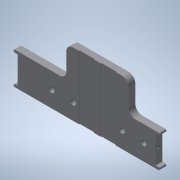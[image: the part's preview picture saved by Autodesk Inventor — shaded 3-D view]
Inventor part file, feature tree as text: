
AUTODESK INVENTOR PART (.ipt)
format: ipt  version: 2022 (Build 260153000, 153)  size: 202,752 bytes
history: native  units: mm
features: sketch x7, extrude x4, fillet x3, hole x3, plane x1, pattern_linear x1
ambient origin geometry x8: Origin, YZ Plane, XZ Plane, XY Plane, X Axis, Y Axis, Z Axis, Center Point
bodies: Volumenkörper1 (feature_tree)
feature tree (19):
  extrude  "Extrusion1"  Depth=24.0mm
  extrude  "Extrusion2"  Depth=23.0mm
  extrude  "Extrusion3"  Depth=2.0mm
  fillet  "Rundung1"  Radius=2.0mm
  fillet  "Rundung2"  Radius=3.0mm
  extrude  "Extrusion4"  Depth=2.0mm
  hole  "Bohrung2"  [1 undecoded]
  hole  "Bohrung3"  [1 undecoded]
  hole  "Bohrung4"  [1 undecoded]
  plane  "Arbeitsebene1"
  pattern_linear  "Rechteckige Anordnung1"  Spacing1=12.0mm  [1 undecoded]
  fillet  "Rundung3"  Radius=26.0mm
  sketch  "Skizze1"  dims[d0=108.0mm d1=24.0mm]
  sketch  "Skizze2"  dims[d2=39.0mm d3=23.0mm]
  sketch  "Skizze3"  dims[d5=5.0mm d6=0.0mm d7=2.0mm d8=2.0mm d9=3.0mm d10=0.0mm]
  sketch  "Skizze4"  dims[d11=2.0mm d12=2.0mm]
  sketch  "Skizze6"  dims[d13=3.0mm d14=0.0mm d15=1.0mm]
  sketch  "Skizze7"  dims[d16=5.0mm d17=11.0mm]
  sketch  "Skizze8"  dims[d18=1.0mm d19=3.0mm d20=0.0mm d31=12.0mm d32=26.0mm d33=26.0mm d34=4.2mm d35=4.2mm d36=8.4mm d37=2.0mm d38=90.0deg d39=8.0mm d40=20.594885mm d41=2.5mm d42=10.0mm d43=2.459mm d44=5.0mm d45=3.023mm d46=2.0mm d47=14.3117mm d48=6.0mm d49=20.594885mm d50=2.5mm d51=10.0mm d52=2.459mm d53=5.0mm d54=3.023mm d55=2.0mm d56=14.3117mm d57=6.0mm d58=20.594885mm d59=23.0mm d60=20.0mm d62=16.0mm d63=2.0mm]
note: 4 required parameter values undecoded (feature->parameter linkage not recoverable at this tier; creation-order binding heuristic only, values carry confidence <= 0.55)
